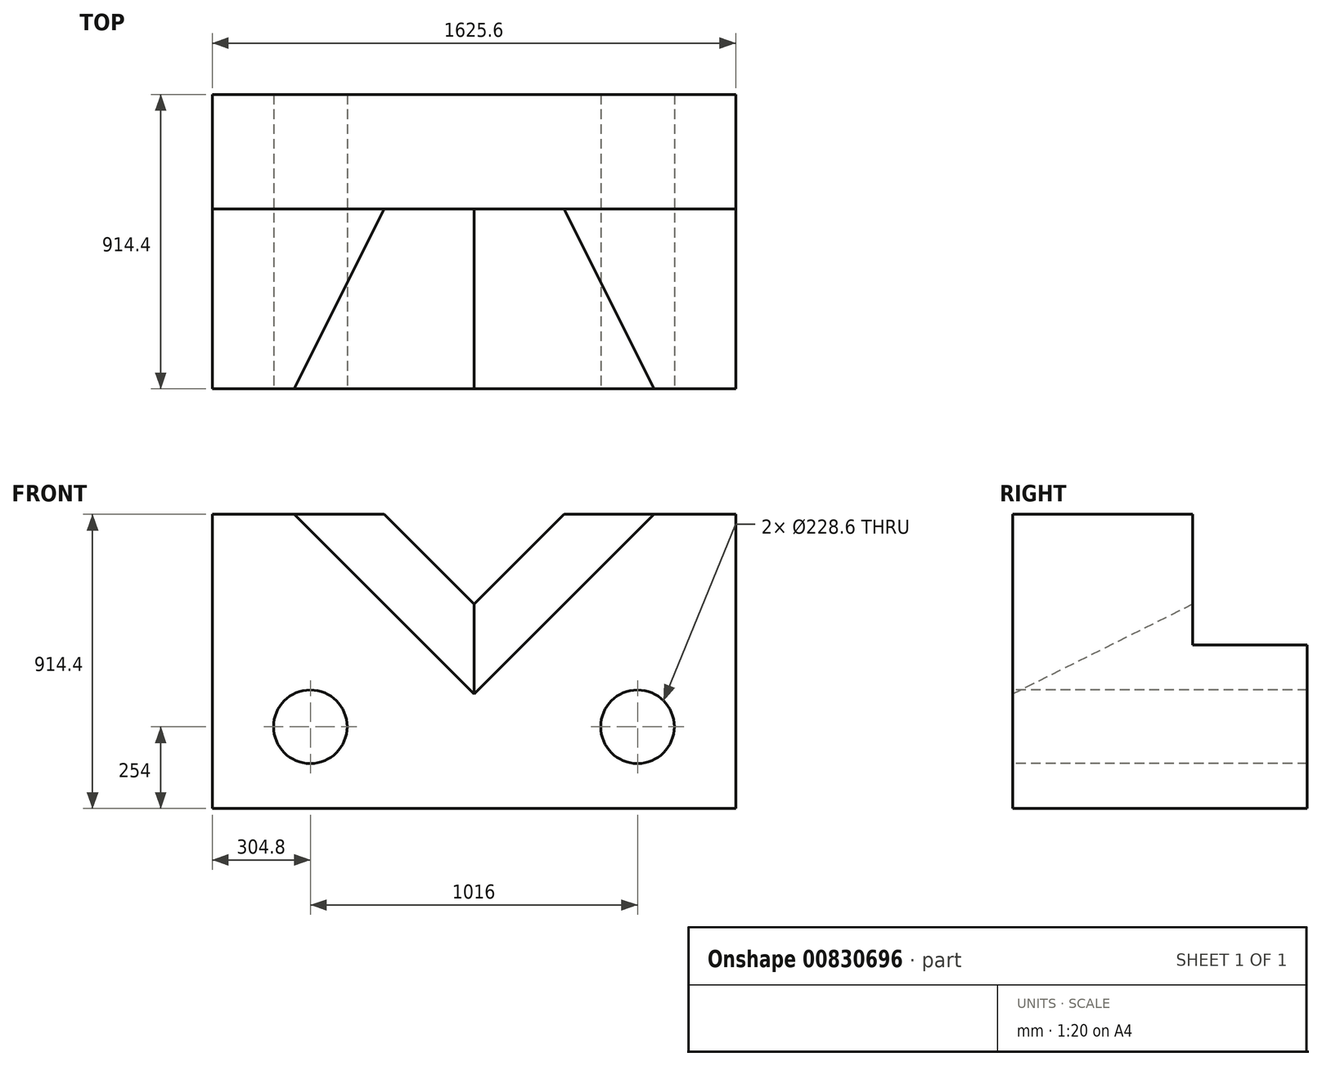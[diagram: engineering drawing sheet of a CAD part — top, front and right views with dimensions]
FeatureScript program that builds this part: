
annotation { "Feature Type Name" : "Feature", "Feature Type Description" : "" }
export const myFeature = defineFeature(function(context is Context, id is Id, definition is map)
    precondition{}
    {
        {
            var Q0;
            Q0=qCreatedBy(makeId("Front.planeOp"),FACE);
            var sketch = newSketch(context, id + "F0", { "sketchPlane" : qUnion([Q0])});
            skLineSegment(sketch, "E0.bottom", {"start": v(-812.8, 914.4) * mm, "end": v(812.8, 914.4) * mm});
            skLineSegment(sketch, "E0.top", {"start": v(-812.8, 0) * mm, "end": v(812.8, 0) * mm});
            skLineSegment(sketch, "E0.left", {"start": v(-812.8, 914.4) * mm, "end": v(-812.8, 0) * mm});
            skLineSegment(sketch, "E0.right", {"start": v(812.8, 914.4) * mm, "end": v(812.8, 0) * mm});
            skSolve(sketch);
        }
        {
            var Q0;
            Q0 = qSketchRegion(id + "F0", true);
            extrude(context, id + "F1", {"entities" : qUnion([Q0]), "oppositeDirection" : true, "depth" : 558.8 * mm, "offsetDistance" : 25.4 * mm});
        }
        {
            var Q0;
            Q0=makeQuery(id+"F1.opExtrude","CAP_FACE",FACE,{"disambiguationData":[OSD([sQuery(id+"F0.wireOp",EDGE,"E0.bottom"),sQuery(id+"F0.wireOp",EDGE,"E0.top"),sQuery(id+"F0.wireOp",EDGE,"E0.left"),sQuery(id+"F0.wireOp",EDGE,"E0.right")])],"isStart":false});
            var sketch = newSketch(context, id + "F2", { "sketchPlane" : qUnion([Q0])});
            skLineSegment(sketch, "E1.bottom", {"start": v(-812.8, 0) * mm, "end": v(812.8, 0) * mm});
            skLineSegment(sketch, "E1.top", {"start": v(-812.8, 508) * mm, "end": v(812.8, 508) * mm});
            skLineSegment(sketch, "E1.left", {"start": v(-812.8, 0) * mm, "end": v(-812.8, 508) * mm});
            skLineSegment(sketch, "E1.right", {"start": v(812.8, 0) * mm, "end": v(812.8, 508) * mm});
            skSolve(sketch);
        }
        {
            var Q0;
            Q0 = qSketchRegion(id + "F2", true);
            extrude(context, id + "F3", {"entities" : qUnion([Q0]), "operationType" : NewBodyOperationType.ADD, "depth" : 355.6 * mm, "offsetDistance" : 25.4 * mm});
        }
        {
            var Q0;
            Q0=makeQuery(id+"F1.opExtrude","CAP_FACE",FACE,{"disambiguationData":[OSD([sQuery(id+"F0.wireOp",EDGE,"E0.bottom"),sQuery(id+"F0.wireOp",EDGE,"E0.top"),sQuery(id+"F0.wireOp",EDGE,"E0.left"),sQuery(id+"F0.wireOp",EDGE,"E0.right")])],"isStart":true});
            var sketch = newSketch(context, id + "F4", { "sketchPlane" : qUnion([Q0])});
            skLineSegment(sketch, "E2", {"start": v(0, 914.4) * mm, "end": v(0, 0) * mm, "construction": true});
            skLineSegment(sketch, "E3", {"start": v(-558.8, 914.4) * mm, "end": v(0, 355.6) * mm});
            skLineSegment(sketch, "E4", {"start": v(0, 355.6) * mm, "end": v(558.8, 914.4) * mm});
            skLineSegment(sketch, "E5", {"start": v(558.8, 914.4) * mm, "end": v(-558.8, 914.4) * mm});
            skSolve(sketch);
        }
        {
            var Q0;
            Q0=makeQuery(id+"F1.opExtrude","CAP_FACE",FACE,{"disambiguationData":[OSD([sQuery(id+"F0.wireOp",EDGE,"E0.bottom"),sQuery(id+"F0.wireOp",EDGE,"E0.top"),sQuery(id+"F0.wireOp",EDGE,"E0.left"),sQuery(id+"F0.wireOp",EDGE,"E0.right")])],"isStart":false});
            var sketch = newSketch(context, id + "F5", { "sketchPlane" : qUnion([Q0])});
            skLineSegment(sketch, "E6", {"start": v(-279.4, 914.4) * mm, "end": v(0, 635) * mm});
            skLineSegment(sketch, "E7", {"start": v(0, 635) * mm, "end": v(279.4, 914.4) * mm});
            skLineSegment(sketch, "E8", {"start": v(279.4, 914.4) * mm, "end": v(-279.4, 914.4) * mm});
            skSolve(sketch);
        }
        {
            var Q1;
            Q1=makeQuery(id+"F5.imprint","IMPRINT",FACE,{"disambiguationData":[TD([[makeQuery(id+"F5.imprint","IMPRINT",EDGE,{"derivedFrom":sQuery(id+"F5.wireOp",EDGE,"E6")}),1.0]])]});
            var Q2;
            Q2=makeQuery(id+"F4.imprint","IMPRINT",FACE,{"disambiguationData":[TD([[makeQuery(id+"F4.imprint","IMPRINT",EDGE,{"derivedFrom":sQuery(id+"F4.wireOp",EDGE,"E3")}),1.0]])]});
            loft(context, id + "F6", {"operationType" : NewBodyOperationType.REMOVE, "sheetProfilesArray" : [{ "sheetProfileEntities" : qUnion([Q1]) }, { "sheetProfileEntities" : qUnion([Q2]) }]});
        }
        {
            var Q0;
            Q0=makeQuery(id+"F1.opExtrude","CAP_FACE",FACE,{"disambiguationData":[OSD([sQuery(id+"F0.wireOp",EDGE,"E0.bottom"),sQuery(id+"F0.wireOp",EDGE,"E0.top"),sQuery(id+"F0.wireOp",EDGE,"E0.left"),sQuery(id+"F0.wireOp",EDGE,"E0.right")])],"isStart":true});
            var sketch = newSketch(context, id + "F7", { "sketchPlane" : qUnion([Q0])});
            skCircle(sketch, "E9", {"center": v(-508, 254) * mm, "radius": 114.3 * mm});
            skLineSegment(sketch, "E10", {"start": v(0, 0) * mm, "end": v(0, 850.5) * mm, "construction": true});
            skCircle(sketch, "E11.MirrorC", {"center": v(508, 254) * mm, "radius": 114.3 * mm});
            skSolve(sketch);
        }
        {
            var Q0;
            Q0 = qSketchRegion(id + "F7", true);
            extrude(context, id + "F8", {"entities" : qUnion([Q0]), "operationType" : NewBodyOperationType.REMOVE, "endBound" : BoundingType.THROUGH_ALL, "oppositeDirection" : true, "depth" : 25.4 * mm, "offsetDistance" : 25.4 * mm});
        }
    });
